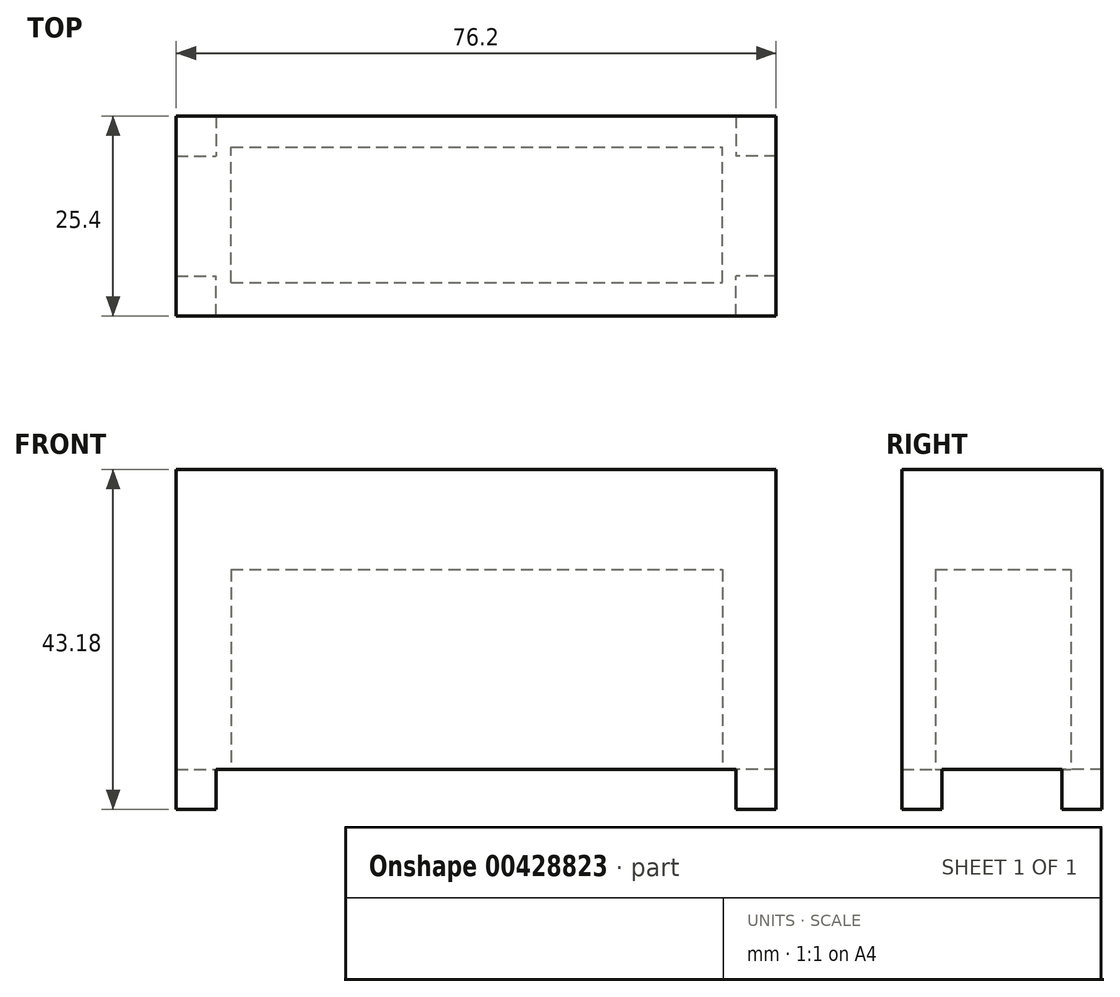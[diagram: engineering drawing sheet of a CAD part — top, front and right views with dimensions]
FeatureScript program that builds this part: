
annotation { "Feature Type Name" : "Feature", "Feature Type Description" : "" }
export const myFeature = defineFeature(function(context is Context, id is Id, definition is map)
    precondition{}
    {
        {
            var Q0;
            Q0=qCreatedBy(makeId("Front.planeOp"),FACE);
            var sketch = newSketch(context, id + "F0", { "sketchPlane" : qUnion([Q0])});
            skLineSegment(sketch, "E0.bottom", {"start": v(0, 0) * mm, "end": v(76.2, 0) * mm});
            skLineSegment(sketch, "E0.top", {"start": v(0, -38.1) * mm, "end": v(76.2, -38.1) * mm});
            skLineSegment(sketch, "E0.left", {"start": v(0, 0) * mm, "end": v(0, -38.1) * mm});
            skLineSegment(sketch, "E0.right", {"start": v(76.2, 0) * mm, "end": v(76.2, -38.1) * mm});
            skSolve(sketch);
        }
        {
            var Q0;
            Q0 = qSketchRegion(id + "F0", true);
            extrude(context, id + "F1", {"entities" : qUnion([Q0]), "depth" : 25.4 * mm});
        }
        {
            var Q0;
            Q0=makeQuery(id+"F1.opExtrude","SWEPT_FACE",FACE,{"disambiguationData":[OSD([sQuery(id+"F0.wireOp",EDGE,"E0.top")])]});
            var sketch = newSketch(context, id + "F2", { "sketchPlane" : qUnion([Q0])});
            skLineSegment(sketch, "E1.bottom", {"start": v(0, 25.4) * mm, "end": v(5.08, 25.4) * mm});
            skLineSegment(sketch, "E1.top", {"start": v(0, 20.32) * mm, "end": v(5.08, 20.32) * mm});
            skLineSegment(sketch, "E1.left", {"start": v(0, 25.4) * mm, "end": v(0, 20.32) * mm});
            skLineSegment(sketch, "E1.right", {"start": v(5.08, 25.4) * mm, "end": v(5.08, 20.32) * mm});
            skLineSegment(sketch, "E2.bottom", {"start": v(0, 0) * mm, "end": v(5.08, 0) * mm});
            skLineSegment(sketch, "E2.top", {"start": v(0, 5.08) * mm, "end": v(5.08, 5.08) * mm});
            skLineSegment(sketch, "E2.left", {"start": v(0, 0) * mm, "end": v(0, 5.08) * mm});
            skLineSegment(sketch, "E2.right", {"start": v(5.08, 0) * mm, "end": v(5.08, 5.08) * mm});
            skLineSegment(sketch, "E3.bottom", {"start": v(76.2, 25.4) * mm, "end": v(71.12, 25.4) * mm});
            skLineSegment(sketch, "E3.top", {"start": v(76.2, 20.32) * mm, "end": v(71.12, 20.32) * mm});
            skLineSegment(sketch, "E3.left", {"start": v(76.2, 25.4) * mm, "end": v(76.2, 20.32) * mm});
            skLineSegment(sketch, "E3.right", {"start": v(71.12, 25.4) * mm, "end": v(71.12, 20.32) * mm});
            skLineSegment(sketch, "E4.bottom", {"start": v(76.2, 0) * mm, "end": v(71.12, 0) * mm});
            skLineSegment(sketch, "E4.top", {"start": v(76.2, 5.08) * mm, "end": v(71.12, 5.08) * mm});
            skLineSegment(sketch, "E4.left", {"start": v(76.2, 0) * mm, "end": v(76.2, 5.08) * mm});
            skLineSegment(sketch, "E4.right", {"start": v(71.12, 0) * mm, "end": v(71.12, 5.08) * mm});
            skSolve(sketch);
        }
        {
            var Q0;
            Q0 = qSketchRegion(id + "F2", true);
            extrude(context, id + "F3", {"entities" : qUnion([Q0]), "operationType" : NewBodyOperationType.ADD, "depth" : 5.08 * mm});
        }
        {
            var Q0;
            {var subQ6=sQuery(id+"F2.wireOp",EDGE,"E1.top");Q0=makeQuery(id+"F2.imprint","IMPRINT",FACE,{"disambiguationData":[TD([[makeQuery(id+"F2.imprint","IMPRINT",EDGE,{"derivedFrom":subQ6}),-1.0]])]});}
            var sketch = newSketch(context, id + "F4", { "sketchPlane" : qUnion([Q0])});
            skLineSegment(sketch, "E5.bottom", {"start": v(7, 21.13) * mm, "end": v(69.37, 21.13) * mm});
            skLineSegment(sketch, "E5.top", {"start": v(7, 3.93) * mm, "end": v(69.37, 3.93) * mm});
            skLineSegment(sketch, "E5.left", {"start": v(7, 21.13) * mm, "end": v(7, 3.93) * mm});
            skLineSegment(sketch, "E5.right", {"start": v(69.37, 21.13) * mm, "end": v(69.37, 3.93) * mm});
            skSolve(sketch);
        }
        {
            var Q0;
            Q0 = qSketchRegion(id + "F4", true);
            extrude(context, id + "F5", {"entities" : qUnion([Q0]), "operationType" : NewBodyOperationType.REMOVE, "oppositeDirection" : true, "depth" : 25.4 * mm});
        }
    });
